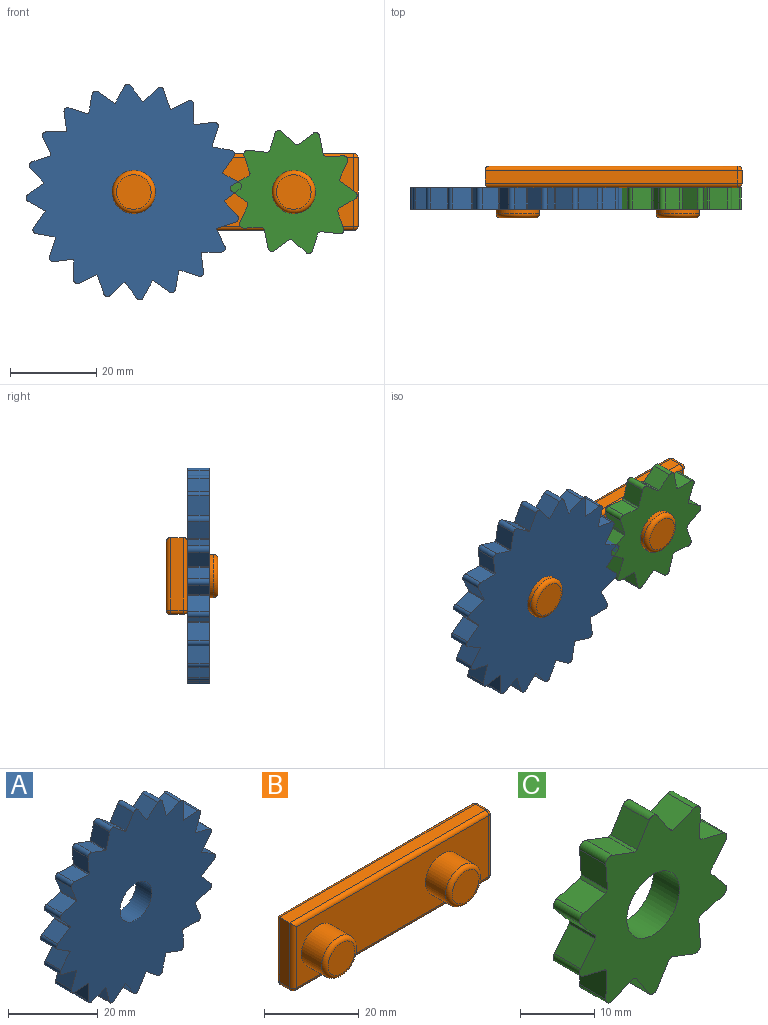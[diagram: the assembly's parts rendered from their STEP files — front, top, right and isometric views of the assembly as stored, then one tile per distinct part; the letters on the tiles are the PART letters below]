
ASSEMBLY  parts=3 mates=2
PART A: 83 faces, bbox 50x5x50 mm
  f0: plane 5x3.78mm, normal (0.85,0,-0.53), area 22.3mm2, adj f1,f79,f81,f82
  f1: cylinder r=21mm len=5mm, axis (0,1,0), area 1.2mm2, adj f0,f2,f81,f82
  f2: plane 5x3.55mm, normal (-0.63,0,-0.78), area 22.8mm2, adj f1,f3,f81,f82
  f3: cylinder r=0.89mm len=5mm, axis (0,1,0), area 8.9mm2, adj f2,f4,f81,f82
  f4: plane 5x4.32mm, normal (0.97,0,-0.24), area 22.3mm2, adj f3,f5,f81,f82
  f5: cylinder r=21mm len=5mm, axis (0,1,0), area 1.2mm2, adj f4,f6,f81,f82
  f6: plane 5x4.26mm, normal (-0.36,0,-0.93), area 22.8mm2, adj f5,f7,f81,f82
  f7: cylinder r=0.89mm len=5mm, axis (0,1,0), area 8.9mm2, adj f6,f8,f81,f82
  f8: plane 5x4.44mm, normal (1,0,0.07), area 22.3mm2, adj f7,f9,f81,f82
  f9: cylinder r=21mm len=5mm, axis (0,1,0), area 1.2mm2, adj f8,f10,f81,f82
  f10: plane 5x4.56mm, normal (-0.05,0,-1), area 22.8mm2, adj f9,f11,f81,f82
  f11: cylinder r=0.89mm len=5mm, axis (0,1,0), area 8.9mm2, adj f10,f12,f81,f82
  f12: plane 5x4.12mm, normal (0.93,0,0.38), area 22.3mm2, adj f11,f13,f81,f82
  f13: cylinder r=21mm len=5mm, axis (0,1,0), area 1.2mm2, adj f12,f14,f81,f82
  f14: plane 5x4.41mm, normal (0.26,0,-0.97), area 22.8mm2, adj f13,f15,f81,f82
  f15: cylinder r=0.89mm len=5mm, axis (0,1,0), area 8.9mm2, adj f14,f16,f81,f82
  f16: plane 5x3.4mm, normal (0.76,0,0.65), area 22.3mm2, adj f15,f17,f81,f82
  f17: cylinder r=21mm len=5mm, axis (0,1,0), area 1.2mm2, adj f16,f18,f81,f82
  f18: plane 5x3.83mm, normal (0.55,0,-0.84), area 22.8mm2, adj f17,f19,f81,f82
  f19: cylinder r=0.89mm len=5mm, axis (0,1,0), area 8.9mm2, adj f18,f20,f81,f82
  f20: plane 5x3.78mm, normal (0.53,0,0.85), area 22.3mm2, adj f19,f21,f81,f82
  f21: cylinder r=21mm len=5mm, axis (0,1,0), area 1.2mm2, adj f20,f22,f81,f82
  f22: plane 5x3.55mm, normal (0.78,0,-0.63), area 22.8mm2, adj f21,f23,f81,f82
  f23: cylinder r=0.89mm len=5mm, axis (0,1,0), area 8.9mm2, adj f22,f24,f81,f82
  f24: plane 5x4.32mm, normal (0.24,0,0.97), area 22.3mm2, adj f23,f25,f81,f82
  f25: cylinder r=21mm len=5mm, axis (0,1,0), area 1.2mm2, adj f24,f26,f81,f82
  f26: plane 5x4.26mm, normal (0.93,0,-0.36), area 22.8mm2, adj f25,f27,f81,f82
  f27: cylinder r=0.89mm len=5mm, axis (0,1,0), area 8.9mm2, adj f26,f28,f81,f82
  f28: plane 5x4.44mm, normal (-0.07,0,1), area 22.3mm2, adj f27,f29,f81,f82
  f29: cylinder r=21mm len=5mm, axis (0,1,0), area 1.2mm2, adj f28,f30,f81,f82
  f30: plane 5x4.56mm, normal (1,0,-0.05), area 22.8mm2, adj f29,f31,f81,f82
  f31: cylinder r=0.89mm len=5mm, axis (0,1,0), area 8.9mm2, adj f30,f32,f81,f82
  f32: plane 5x4.12mm, normal (-0.38,0,0.93), area 22.3mm2, adj f31,f33,f81,f82
  f33: cylinder r=21mm len=5mm, axis (0,1,0), area 1.2mm2, adj f32,f34,f81,f82
  f34: plane 5x4.41mm, normal (0.97,0,0.26), area 22.8mm2, adj f33,f35,f81,f82
  f35: cylinder r=0.89mm len=5mm, axis (0,1,0), area 8.9mm2, adj f34,f36,f81,f82
  f36: plane 5x3.4mm, normal (-0.65,0,0.76), area 22.3mm2, adj f35,f37,f81,f82
  f37: cylinder r=21mm len=5mm, axis (0,1,0), area 1.2mm2, adj f36,f38,f81,f82
  f38: plane 5x3.83mm, normal (0.84,0,0.55), area 22.8mm2, adj f37,f39,f81,f82
  f39: cylinder r=0.89mm len=5mm, axis (0,1,0), area 8.9mm2, adj f38,f40,f81,f82
  f40: plane 5x3.78mm, normal (-0.85,0,0.53), area 22.3mm2, adj f39,f41,f81,f82
  f41: cylinder r=21mm len=5mm, axis (0,1,0), area 1.2mm2, adj f40,f42,f81,f82
  f42: plane 5x3.55mm, normal (0.63,0,0.78), area 22.8mm2, adj f41,f43,f81,f82
  f43: cylinder r=0.89mm len=5mm, axis (0,1,0), area 8.9mm2, adj f42,f44,f81,f82
  f44: plane 5x4.32mm, normal (-0.97,0,0.24), area 22.3mm2, adj f43,f45,f81,f82
  f45: cylinder r=21mm len=5mm, axis (0,1,0), area 1.2mm2, adj f44,f46,f81,f82
  f46: plane 5x4.26mm, normal (0.36,0,0.93), area 22.8mm2, adj f45,f47,f81,f82
  f47: cylinder r=0.89mm len=5mm, axis (0,1,0), area 8.9mm2, adj f46,f48,f81,f82
  f48: plane 5x4.44mm, normal (-1,0,-0.07), area 22.3mm2, adj f47,f49,f81,f82
  f49: cylinder r=21mm len=5mm, axis (0,1,0), area 1.2mm2, adj f48,f50,f81,f82
  f50: plane 5x4.56mm, normal (0.05,0,1), area 22.8mm2, adj f49,f51,f81,f82
  f51: cylinder r=0.89mm len=5mm, axis (0,1,0), area 8.9mm2, adj f50,f52,f81,f82
  f52: plane 5x4.12mm, normal (-0.93,0,-0.38), area 22.3mm2, adj f51,f53,f81,f82
  f53: cylinder r=21mm len=5mm, axis (0,1,0), area 1.2mm2, adj f52,f54,f81,f82
  f54: plane 5x4.41mm, normal (-0.26,0,0.97), area 22.8mm2, adj f53,f55,f81,f82
  f55: cylinder r=0.89mm len=5mm, axis (0,1,0), area 8.9mm2, adj f54,f56,f81,f82
  f56: plane 5x3.4mm, normal (-0.76,0,-0.65), area 22.3mm2, adj f55,f57,f81,f82
  f57: cylinder r=21mm len=5mm, axis (0,1,0), area 1.2mm2, adj f56,f58,f81,f82
  f58: plane 5x3.83mm, normal (-0.55,0,0.84), area 22.8mm2, adj f57,f59,f81,f82
  f59: cylinder r=0.89mm len=5mm, axis (0,1,0), area 8.9mm2, adj f58,f60,f81,f82
  f60: plane 5x3.78mm, normal (-0.53,0,-0.85), area 22.3mm2, adj f59,f61,f81,f82
  f61: cylinder r=21mm len=5mm, axis (0,1,0), area 1.2mm2, adj f60,f62,f81,f82
  f62: plane 5x3.55mm, normal (-0.78,0,0.63), area 22.8mm2, adj f61,f63,f81,f82
  f63: cylinder r=0.89mm len=5mm, axis (0,1,0), area 8.9mm2, adj f62,f64,f81,f82
  f64: plane 5x4.32mm, normal (-0.24,0,-0.97), area 22.3mm2, adj f63,f65,f81,f82
  f65: cylinder r=21mm len=5mm, axis (0,1,0), area 1.2mm2, adj f64,f66,f81,f82
  f66: plane 5x4.26mm, normal (-0.93,0,0.36), area 22.8mm2, adj f65,f67,f81,f82
  f67: cylinder r=0.89mm len=5mm, axis (0,1,0), area 8.9mm2, adj f66,f68,f81,f82
  f68: plane 5x4.44mm, normal (0.07,0,-1), area 22.3mm2, adj f67,f69,f81,f82
  f69: cylinder r=21mm len=5mm, axis (0,1,0), area 1.2mm2, adj f68,f70,f81,f82
  f70: plane 5x4.56mm, normal (-1,0,0.05), area 22.8mm2, adj f69,f71,f81,f82
  f71: cylinder r=0.89mm len=5mm, axis (0,1,0), area 8.9mm2, adj f70,f72,f81,f82
  f72: plane 5x4.12mm, normal (0.38,0,-0.93), area 22.3mm2, adj f71,f73,f81,f82
  f73: cylinder r=21mm len=5mm, axis (0,1,0), area 1.2mm2, adj f72,f74,f81,f82
  f74: plane 5x4.41mm, normal (-0.97,0,-0.26), area 22.8mm2, adj f73,f75,f81,f82
  f75: cylinder r=0.89mm len=5mm, axis (0,1,0), area 8.9mm2, adj f74,f76,f81,f82
  f76: plane 5x3.4mm, normal (0.65,0,-0.76), area 22.3mm2, adj f75,f77,f81,f82
  f77: cylinder r=21mm len=5mm, axis (0,1,0), area 1.2mm2, adj f76,f78,f81,f82
  f78: plane 5x3.83mm, normal (-0.84,0,-0.55), area 22.8mm2, adj f77,f79,f81,f82
  f79: cylinder r=0.89mm len=5mm, axis (0,1,0), area 8.9mm2, adj f0,f78,f81,f82
  f80: cylinder r=5mm len=10mm, axis (0,1,0), area 157.1mm2, adj f81,f82
  f81: plane 49.95x49.95mm, normal (0,-1,0), area 1593.1mm2, adj f0,f1,f2,f3,f4,f5,f6,f7
  f82: plane 49.95x49.95mm, normal (0,1,0), area 1593.1mm2, adj f0,f1,f2,f3,f4,f5,f6,f7
PART B: 29 faces, bbox 59.4x12x17.8 mm
  f0: cylinder r=5mm len=10mm, axis (0,1,0), area 188.5mm2, adj f8,f28
  f1: plane 8x8mm, normal (0,-1,0), area 50.3mm2, adj f28
  f2: cylinder r=5mm len=10mm, axis (0,1,0), area 188.5mm2, adj f8,f27
  f3: plane 8x8mm, normal (0,-1,0), area 50.3mm2, adj f27
  f4: plane 57.4x3mm, normal (0,0,-1), area 172.2mm2, adj f15,f20,f23,f26
  f5: plane 15.76x3mm, normal (1,0,0), area 47.3mm2, adj f12,f21,f22,f26
  f6: plane 58.4x3mm, normal (0,0,1), area 175.2mm2, adj f7,f11,f12,f13
  f7: plane 16.76x3mm, normal (-1,0,0), area 50.3mm2, adj f6,f10,f14,f15
  f8: plane 57.4x15.76mm, normal (0,-1,0), area 747.8mm2, adj f0,f2,f10,f11,f20,f21
  f9: plane 57.4x15.76mm, normal (0,1,0), area 904.9mm2, adj f13,f14,f22,f23
  f10: cylinder r=1mm len=16.76mm, axis (0,0,1), area 25.8mm2, adj f7,f8,f11,f16
  f11: cylinder r=1mm len=58.4mm, axis (1,0,0), area 91.2mm2, adj f6,f8,f10,f17
  f12: cylinder r=1mm len=3mm, axis (0,1,0), area 4.7mm2, adj f5,f6,f17,f18
  f13: cylinder r=1mm len=58.4mm, axis (-1,0,0), area 91.2mm2, adj f6,f9,f14,f18
  f14: cylinder r=1mm len=16.76mm, axis (0,0,-1), area 25.8mm2, adj f7,f9,f13,f19
  f15: cylinder r=1mm len=3mm, axis (0,1,0), area 4.7mm2, adj f4,f7,f16,f19
  f16: sphere r=1mm, area 1.6mm2, adj f10,f15,f20
  f17: sphere r=1mm, area 1.6mm2, adj f11,f12,f21
  f18: sphere r=1mm, area 1.6mm2, adj f12,f13,f22
  f19: sphere r=1mm, area 1.6mm2, adj f14,f15,f23
  f20: cylinder r=1mm len=57.4mm, axis (-1,0,0), area 90.2mm2, adj f4,f8,f16,f24
  f21: cylinder r=1mm len=15.76mm, axis (0,0,-1), area 24.8mm2, adj f5,f8,f17,f24
  f22: cylinder r=1mm len=15.76mm, axis (0,0,1), area 24.8mm2, adj f5,f9,f18,f25
  f23: cylinder r=1mm len=57.4mm, axis (1,0,0), area 90.2mm2, adj f4,f9,f19,f25
  f24: sphere r=1mm, area 1.6mm2, adj f20,f21,f26
  f25: sphere r=1mm, area 1.6mm2, adj f22,f23,f26
  f26: cylinder r=1mm len=3mm, axis (0,-1,0), area 4.7mm2, adj f4,f5,f24,f25
  f27: torus R=4mm, axis (0,-1,0), area 45.8mm2, adj f2,f3
  f28: torus R=4mm, axis (0,-1,0), area 45.8mm2, adj f0,f1
PART C: 43 faces, bbox 28x5x29.4 mm
  f0: plane 5x3.7mm, normal (0.85,0,-0.53), area 21.7mm2, adj f1,f39,f41,f42
  f1: cylinder r=11mm len=5mm, axis (0,1,0), area 2.7mm2, adj f0,f2,f41,f42
  f2: plane 5x4.19mm, normal (-0.36,0,-0.93), area 22.4mm2, adj f1,f3,f41,f42
  f3: cylinder r=0.91mm len=5mm, axis (0,1,0), area 9.2mm2, adj f2,f4,f41,f42
  f4: plane 5x4.34mm, normal (1,0,0.07), area 21.7mm2, adj f3,f5,f41,f42
  f5: cylinder r=11mm len=5mm, axis (0,1,0), area 2.7mm2, adj f4,f6,f41,f42
  f6: plane 5x4.33mm, normal (0.26,0,-0.97), area 22.4mm2, adj f5,f7,f41,f42
  f7: cylinder r=0.91mm len=5mm, axis (0,1,0), area 9.2mm2, adj f6,f8,f41,f42
  f8: plane 5x3.32mm, normal (0.76,0,0.65), area 21.7mm2, adj f7,f9,f41,f42
  f9: cylinder r=11mm len=5mm, axis (0,1,0), area 2.7mm2, adj f8,f10,f41,f42
  f10: plane 5x3.49mm, normal (0.78,0,-0.63), area 22.4mm2, adj f9,f11,f41,f42
  f11: cylinder r=0.91mm len=5mm, axis (0,1,0), area 9.2mm2, adj f10,f12,f41,f42
  f12: plane 5x4.22mm, normal (0.24,0,0.97), area 21.7mm2, adj f11,f13,f41,f42
  f13: cylinder r=11mm len=5mm, axis (0,1,0), area 2.7mm2, adj f12,f14,f41,f42
  f14: plane 5x4.48mm, normal (1,0,-0.05), area 22.4mm2, adj f13,f15,f41,f42
  f15: cylinder r=0.91mm len=5mm, axis (0,1,0), area 9.2mm2, adj f14,f16,f41,f42
  f16: plane 5x4.03mm, normal (-0.38,0,0.93), area 21.7mm2, adj f15,f17,f41,f42
  f17: cylinder r=11mm len=5mm, axis (0,1,0), area 2.7mm2, adj f16,f18,f41,f42
  f18: plane 5x3.76mm, normal (0.84,0,0.55), area 22.4mm2, adj f17,f19,f41,f42
  f19: cylinder r=0.91mm len=5mm, axis (0,1,0), area 9.2mm2, adj f18,f20,f41,f42
  f20: plane 5x3.7mm, normal (-0.85,0,0.53), area 21.7mm2, adj f19,f21,f41,f42
  f21: cylinder r=11mm len=5mm, axis (0,1,0), area 2.7mm2, adj f20,f22,f41,f42
  f22: plane 5x4.19mm, normal (0.36,0,0.93), area 22.4mm2, adj f21,f23,f41,f42
  f23: cylinder r=0.91mm len=5mm, axis (0,1,0), area 9.2mm2, adj f22,f24,f41,f42
  f24: plane 5x4.34mm, normal (-1,0,-0.07), area 21.7mm2, adj f23,f25,f41,f42
  f25: cylinder r=11mm len=5mm, axis (0,1,0), area 2.7mm2, adj f24,f26,f41,f42
  f26: plane 5x4.33mm, normal (-0.26,0,0.97), area 22.4mm2, adj f25,f27,f41,f42
  f27: cylinder r=0.91mm len=5mm, axis (0,1,0), area 9.2mm2, adj f26,f28,f41,f42
  f28: plane 5x3.32mm, normal (-0.76,0,-0.65), area 21.7mm2, adj f27,f29,f41,f42
  f29: cylinder r=11mm len=5mm, axis (0,1,0), area 2.7mm2, adj f28,f30,f41,f42
  f30: plane 5x3.49mm, normal (-0.78,0,0.63), area 22.4mm2, adj f29,f31,f41,f42
  f31: cylinder r=0.91mm len=5mm, axis (0,1,0), area 9.2mm2, adj f30,f32,f41,f42
  f32: plane 5x4.22mm, normal (-0.24,0,-0.97), area 21.7mm2, adj f31,f33,f41,f42
  f33: cylinder r=11mm len=5mm, axis (0,1,0), area 2.7mm2, adj f32,f34,f41,f42
  f34: plane 5x4.48mm, normal (-1,0,0.05), area 22.4mm2, adj f33,f35,f41,f42
  f35: cylinder r=0.91mm len=5mm, axis (0,1,0), area 9.2mm2, adj f34,f36,f41,f42
  f36: plane 5x4.03mm, normal (0.38,0,-0.93), area 21.7mm2, adj f35,f37,f41,f42
  f37: cylinder r=11mm len=5mm, axis (0,1,0), area 2.7mm2, adj f36,f38,f41,f42
  f38: plane 5x3.76mm, normal (-0.84,0,-0.55), area 22.4mm2, adj f37,f39,f41,f42
  f39: cylinder r=0.91mm len=5mm, axis (0,1,0), area 9.2mm2, adj f0,f38,f41,f42
  f40: cylinder r=5mm len=10mm, axis (0,1,0), area 157.1mm2, adj f41,f42
  f41: plane 29.39x28.05mm, normal (0,-1,0), area 432.9mm2, adj f0,f1,f2,f3,f4,f5,f6,f7
  f42: plane 29.39x28.05mm, normal (0,1,0), area 432.9mm2, adj f0,f1,f2,f3,f4,f5,f6,f7
PLACE A rot(axis=(0,-1,0),21.4deg) t=(-33.92,-10.19,-1.35)mm
PLACE B t=(-11.77,-5.19,-1.35)mm fixed
PLACE C rot(axis=(0,1,0),21.4deg) t=(3.08,-10.19,-1.35)mm
MATE revolute A.f80 <-> B.f0  axis (0,1,0) through (-33.92,-10.19,-1.35)mm
MATE revolute C.f40 <-> B.f2  axis (0,1,0) through (3.08,-10.19,-1.35)mm
